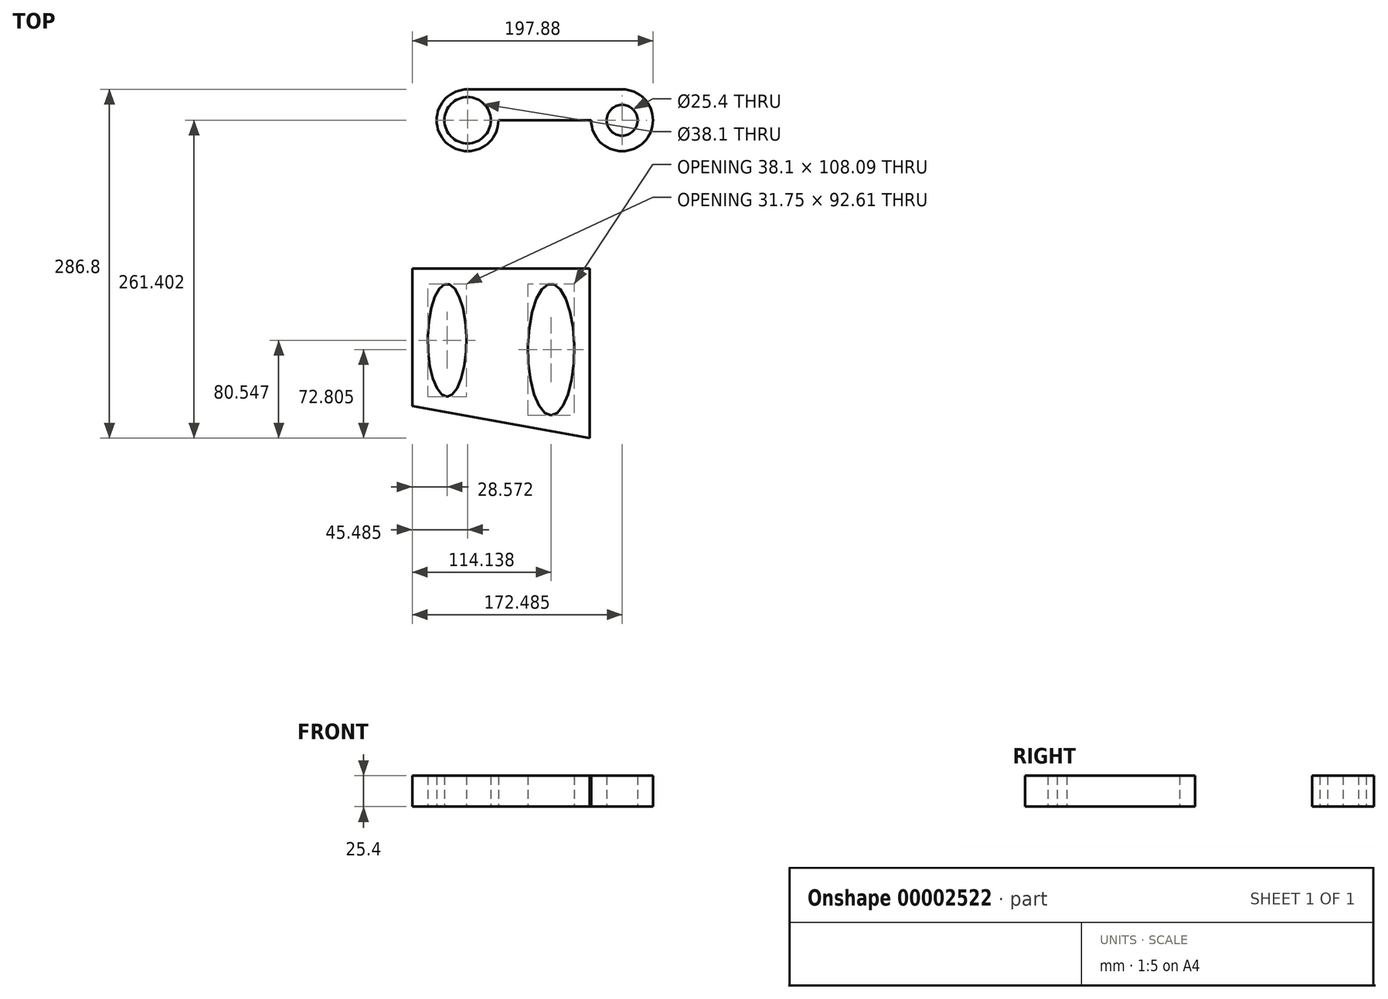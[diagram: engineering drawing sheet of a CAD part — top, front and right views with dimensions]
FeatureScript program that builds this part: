
annotation { "Feature Type Name" : "Feature", "Feature Type Description" : "" }
export const myFeature = defineFeature(function(context is Context, id is Id, definition is map)
    precondition{}
    {
        {
            var Q0;
            Q0=qCreatedBy(makeId("Top.planeOp"),FACE);
            var sketch = newSketch(context, id + "F0", { "sketchPlane" : qUnion([Q0])});
            skLineSegment(sketch, "E0", {"start": v(-93.17, 31.68) * mm, "end": v(33.83, 31.68) * mm});
            skLineSegment(sketch, "E1", {"start": v(-67.77, 6.28) * mm, "end": v(8.43, 6.28) * mm});
            skArc(sketch, "E2", {"start": v(8.43, 6.28) * mm, "mid": v(51.8, -11.68) * mm, "end": v(33.83, 31.68) * mm});
            skArc(sketch, "E3", {"start": v(-93.17, 31.68) * mm, "mid": v(-111.13, -11.68) * mm, "end": v(-67.77, 6.28) * mm});
            skCircle(sketch, "E4", {"center": v(33.83, 6.28) * mm, "radius": 12.7 * mm});
            skCircle(sketch, "E5", {"center": v(-93.17, 6.28) * mm, "radius": 19.05 * mm});
            skSolve(sketch);
        }
        {
            var Q0;
            Q0 = qSketchRegion(id + "F0", true);
            extrude(context, id + "F1", {"entities" : qUnion([Q0]), "depth" : 25.4 * mm});
        }
        {
            var Q0;
            Q0=qCreatedBy(makeId("Top.planeOp"),FACE);
            var sketch = newSketch(context, id + "F2", { "sketchPlane" : qUnion([Q0])});
            skLineSegment(sketch, "E6", {"start": v(-138.65, -115.57) * mm, "end": v(-138.65, -228.7) * mm});
            skLineSegment(sketch, "E7", {"start": v(-138.65, -228.7) * mm, "end": v(7.16, -255.12) * mm});
            skLineSegment(sketch, "E8", {"start": v(7.16, -255.12) * mm, "end": v(7.16, -115.57) * mm});
            skLineSegment(sketch, "E9", {"start": v(7.16, -115.57) * mm, "end": v(-138.65, -115.57) * mm});
            skLineSegment(sketch, "E10", {"start": v(-138.65, -128.27) * mm, "end": v(7.16, -128.27) * mm, "construction": true});
            skEllipse(sketch, "E11", {"center": v(-110.08, -174.57) * mm, "majorRadius": 46.3 * mm, "minorRadius": 15.88 * mm, "majorAxis": v(0, -1)});
            skLineSegment(sketch, "E12", {"start": v(-138.65, -215.79) * mm, "end": v(7.16, -242.21) * mm, "construction": true});
            skEllipse(sketch, "E13", {"center": v(-24.51, -182.31) * mm, "majorRadius": 54.05 * mm, "minorRadius": 19.05 * mm, "majorAxis": v(0, -1)});
            skLineSegment(sketch, "E14", {"start": v(-125.95, -128.27) * mm, "end": v(-125.95, -218.1) * mm, "construction": true});
            skLineSegment(sketch, "E15", {"start": v(-5.54, -128.27) * mm, "end": v(-5.54, -239.91) * mm, "construction": true});
            skSolve(sketch);
        }
        {
            var Q0;
            Q0 = qSketchRegion(id + "F2", true);
            extrude(context, id + "F3", {"entities" : qUnion([Q0]), "depth" : 25.4 * mm});
        }
    });
